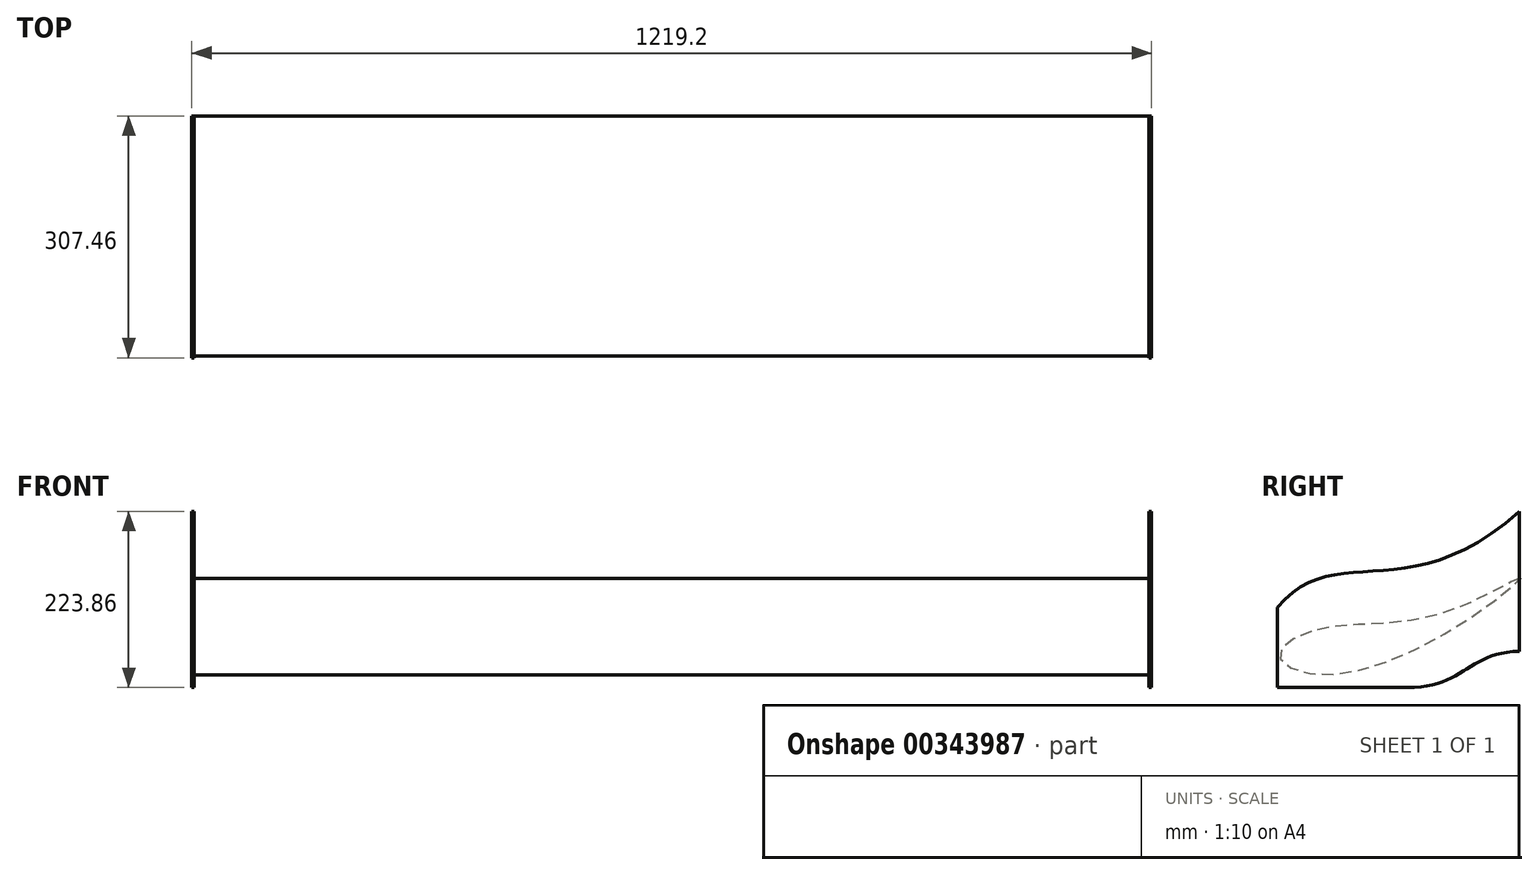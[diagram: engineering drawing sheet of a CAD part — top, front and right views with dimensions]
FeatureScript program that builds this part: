
annotation { "Feature Type Name" : "Feature", "Feature Type Description" : "" }
export const myFeature = defineFeature(function(context is Context, id is Id, definition is map)
    precondition{}
    {
        {
            var Q0;
            Q0=qCreatedBy(makeId("Right.planeOp"),FACE);
            var sketch = newSketch(context, id + "F0", { "sketchPlane" : qUnion([Q0])});
            skFitSpline(sketch, "E0", {"points": [v(0, 0) * mm, v(-102.16, -45.85) * mm, v(-255.27, -64.61) * mm, v(-304.8, -97.64) * mm, v(-250.01, -122.4) * mm, v(-66.14, -52.6) * mm, v(0, 0) * mm]});
            skSolve(sketch);
        }
        {
            var Q0;
            Q0=qCreatedBy(makeId("Right.planeOp"),FACE);
            var sketch = newSketch(context, id + "F1", { "sketchPlane" : qUnion([Q0])});
            skLineSegment(sketch, "E1", {"start": v(-307.22, -98.13) * mm, "end": v(-307.22, -138.7) * mm});
            skFitSpline(sketch, "E2", {"points": [v(-307.22, -37.1) * mm, v(0, 85.16) * mm], "startDerivative": vector(215.23, 265.33) * mm, "endDerivative": vector(423.55, 379.36) * mm});
            skLineSegment(sketch, "E3", {"start": v(-307.22, -98.13) * mm, "end": v(-307.22, -37.1) * mm});
            skLineSegment(sketch, "E4", {"start": v(0, 85.16) * mm, "end": v(0, -92.64) * mm});
            skLineSegment(sketch, "E5", {"start": v(-307.22, -138.7) * mm, "end": v(-142.12, -138.7) * mm});
            skFitSpline(sketch, "E6", {"points": [v(-142.12, -138.7) * mm, v(0, -92.64) * mm], "startDerivative": vector(212.7, -2.2) * mm, "endDerivative": vector(195.5, 2.2) * mm});
            skSolve(sketch);
        }
        {
            var Q0;
            Q0 = qSketchRegion(id + "F1", true);
            extrude(context, id + "F2", {"entities" : qUnion([Q0]), "depth" : 3.17 * mm});
        }
        {
            var Q0;
            Q0 = qSketchRegion(id + "F0", true);
            extrude(context, id + "F3", {"entities" : qUnion([Q0]), "operationType" : NewBodyOperationType.ADD, "depth" : 609.6 * mm, "offsetDistance" : 25.4 * mm});
        }
        {
            var Q0;
            Q0=makeQuery(id+"F2.opExtrude","SWEPT_BODY",BODY,{"disambiguationData":[OSD([sQuery(id+"F1.wireOp",EDGE,"E1"),sQuery(id+"F1.wireOp",EDGE,"E2"),sQuery(id+"F1.wireOp",EDGE,"E3"),sQuery(id+"F1.wireOp",EDGE,"E4"),sQuery(id+"F1.wireOp",EDGE,"E5"),sQuery(id+"F1.wireOp",EDGE,"E6")])]});
            var Q1;
            Q1=makeQuery(id+"F3.opExtrude","CAP_FACE",FACE,{"disambiguationData":[OSD([sQuery(id+"F0.wireOp",EDGE,"E0")])],"isStart":false});
            mirror(context, id + "F4", {"operationType" : NewBodyOperationType.ADD, "entities" : qUnion([Q0]), "mirrorPlane" : qUnion([Q1])});
        }
    });
